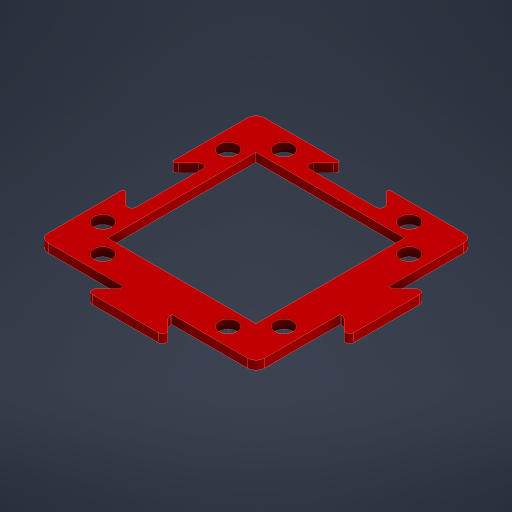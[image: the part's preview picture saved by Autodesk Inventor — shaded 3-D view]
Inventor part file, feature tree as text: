
AUTODESK INVENTOR PART (.ipt)
format: ipt  version: 2023.4 (Build 274418000, 418)  size: 402,432 bytes
history: native  units: mm
features: reference x9, extrude x3, other x3, sketch x2, fillet x1, projected_geometry x1
ambient origin geometry x8: Origin, YZ Plane, XZ Plane, XY Plane, X Axis, Y Axis, Z Axis, Center Point
bodies: Solid1 (feature_tree)
feature tree (19):
  extrude  "Extrusion1"  Depth=2.0mm TaperAngle=0.0deg
  sketch  "Sketch2"  dims[d16=10.0mm d17=0.0mm d18=0.25mm d19=20.0mm d20=10.0mm d21=45.0deg d22=1.0mm d23=1.5mm d24=1.0mm d25=0.075mm d28=15.171573mm d29=2.87868mm d30=2.87868mm d31=20.0mm d32=10.0mm d33=45.0deg d34=1.0mm d35=1.5mm d36=1.0mm d37=0.075mm d38=15.171573mm d39=2.87868mm d40=2.87868mm d41=0.25mm d42=0.0mm d43=40.0mm d45=360.0deg]
  extrude  "Extrusion2"  Depth=0.25mm
  extrude  "Extrusion3"  Depth=0.25mm
  fillet  "Fillet1"  Radius=2.87868mm
  sketch  "Sketch1"  dims[d0=2.0mm d1=0.0mm d14=2.0mm d15=0.0mm]
  reference  "Reference1"
  reference  "Reference2"
  reference  "Reference3"
  reference  "Reference4"
  reference  "Reference5"
  reference  "Reference6"
  reference  "Reference7"
  reference  "Reference8"
  reference  "Reference9"
  projected_geometry  "Projected Loop2"
  other  "<path>\Projects\Project Protocube\Protocube\CAD, STL, OBJ Files\1 CAD\Cube 1x1 V5.iam"
  other  "Cube 1x1 V5.iam"
  other  "Cube 1x1 Top V5:1"
note: 1 file-system path scrubbed to <path> (originals preserved in map.json)
